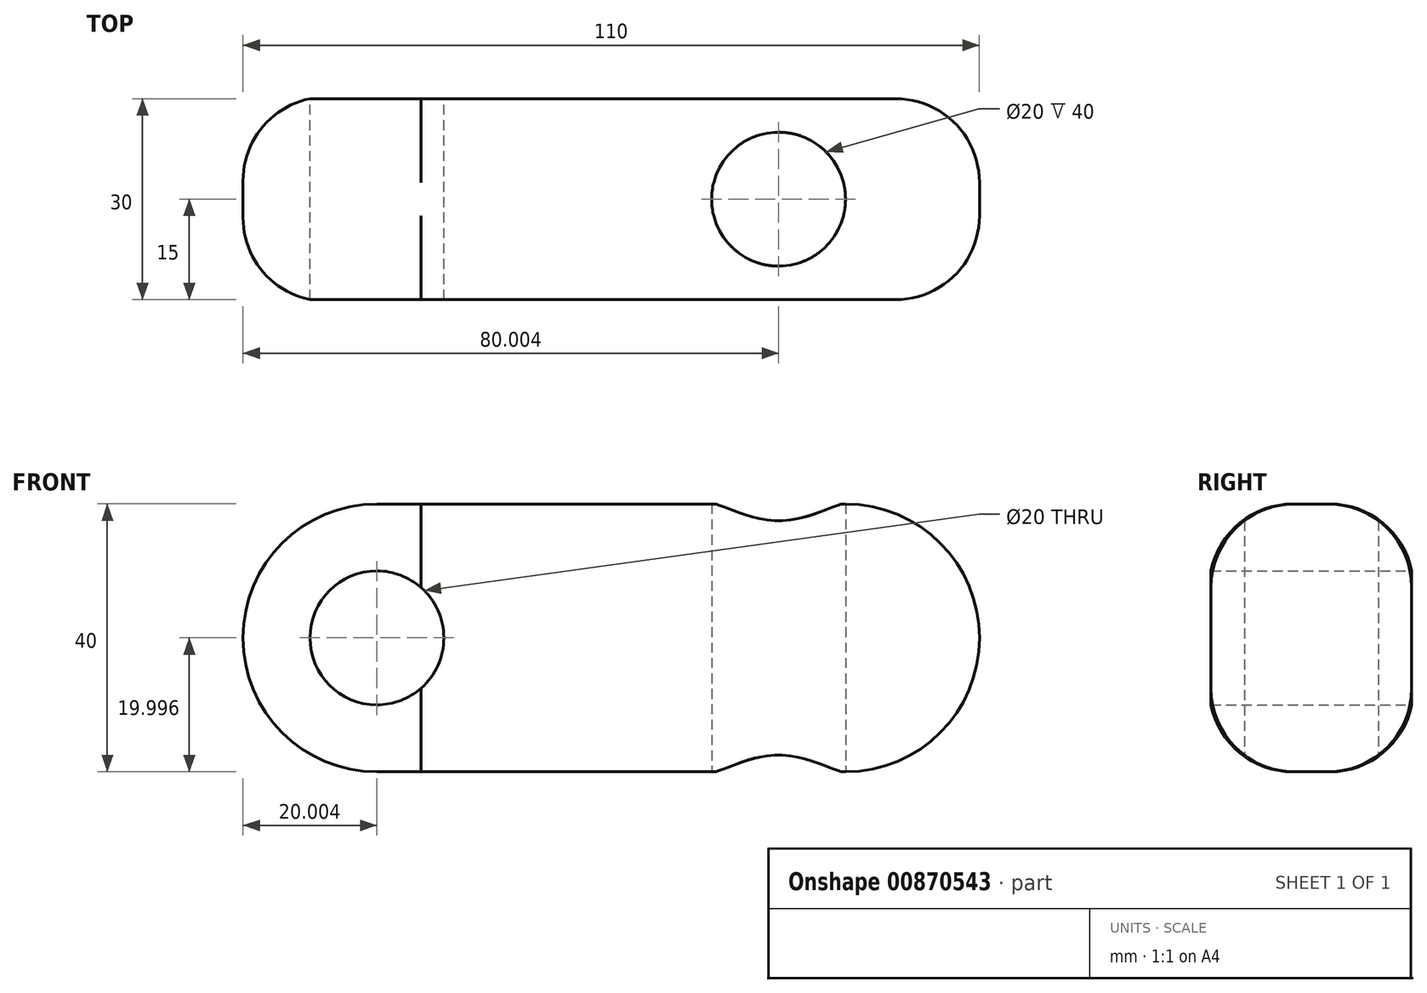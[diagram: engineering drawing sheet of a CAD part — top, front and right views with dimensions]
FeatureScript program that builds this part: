
annotation { "Feature Type Name" : "Feature", "Feature Type Description" : "" }
export const myFeature = defineFeature(function(context is Context, id is Id, definition is map)
    precondition{}
    {
        {
            var Q0;
            Q0=qCreatedBy(makeId("Front.planeOp"),FACE);
            var sketch = newSketch(context, id + "F0", { "sketchPlane" : qUnion([Q0])});
            skLineSegment(sketch, "E0.bottom", {"start": v(-58.02, 21.1) * mm, "end": v(11.98, 21.1) * mm});
            skLineSegment(sketch, "E0.top", {"start": v(-58.02, -18.9) * mm, "end": v(11.98, -18.9) * mm});
            skLineSegment(sketch, "E0.left", {"start": v(-78.02, 1.1) * mm, "end": v(-78.02, 1.1) * mm});
            skLineSegment(sketch, "E0.right", {"start": v(31.98, 1.1) * mm, "end": v(31.98, 1.1) * mm});
            skPoint(sketch, "E1", {"position": v(11.98, 0) * mm});
            skPoint(sketch, "E2.visualSharp", {"position": v(-78.02, 21.1) * mm});
            skArc(sketch, "E2.filletArc", {"start": v(-58.02, 21.1) * mm, "mid": v(-72.16, 15.25) * mm, "end": v(-78.02, 1.1) * mm});
            skPoint(sketch, "E3.visualSharp", {"position": v(-78.02, -18.9) * mm});
            skArc(sketch, "E3.filletArc", {"start": v(-78.02, 1.1) * mm, "mid": v(-72.16, -13.04) * mm, "end": v(-58.02, -18.9) * mm});
            skPoint(sketch, "E4.visualSharp", {"position": v(31.98, -18.9) * mm});
            skArc(sketch, "E4.filletArc", {"start": v(11.98, -18.9) * mm, "mid": v(26.13, -13.04) * mm, "end": v(31.98, 1.1) * mm});
            skPoint(sketch, "E5.visualSharp", {"position": v(31.98, 21.1) * mm});
            skArc(sketch, "E5.filletArc", {"start": v(31.98, 1.1) * mm, "mid": v(26.13, 15.25) * mm, "end": v(11.98, 21.1) * mm});
            skCircle(sketch, "E6", {"center": v(-58.02, 1.1) * mm, "radius": 10 * mm});
            skSolve(sketch);
        }
        {
            var Q0;
            Q0=makeQuery(id+"F0.imprint","IMPRINT",FACE,{"disambiguationData":[TD([[makeQuery(id+"F0.imprint","IMPRINT",EDGE,{"derivedFrom":sQuery(id+"F0.wireOp",EDGE,"E0.bottom")}),-1.0]])]});
            extrude(context, id + "F1", {"entities" : qUnion([Q0]), "depth" : 30 * mm, "offsetDistance" : 25 * mm});
        }
        {
            var Q0;
            Q0=makeQuery(id+"F1.opExtrude","SWEPT_FACE",FACE,{"disambiguationData":[OSD([sQuery(id+"F0.wireOp",EDGE,"E0.top")])]});
            var sketch = newSketch(context, id + "F2", { "sketchPlane" : qUnion([Q0])});
            skCircle(sketch, "E7", {"center": v(1.98, 15) * mm, "radius": 10 * mm});
            skPoint(sketch, "E7.centerSnap0", {"position": v(11.98, 15) * mm});
            skSolve(sketch);
        }
        {
            var Q0;
            Q0=makeQuery(id+"F1.opExtrude","CAP_EDGE",EDGE,{"disambiguationData":[OSD([sQuery(id+"F0.wireOp",EDGE,"E0.bottom")])],"isStart":true});
            var Q1;
            Q1=makeQuery(id+"F1.opExtrude","CAP_EDGE",EDGE,{"disambiguationData":[OSD([sQuery(id+"F0.wireOp",EDGE,"E0.bottom")])],"isStart":false});
            fillet(context, id + "F3", {"entities" : qUnion([Q0, Q1]), "radius" : 12.5 * mm, "tangentPropagation" : true, "allowEdgeOverflow" : false});
        }
        {
            var Q0;
            Q0=sQuery(id+"F2.wireOp",VERTEX,"E7.center");
            var Q1;
            Q1=makeQuery(id+"F1.opExtrude","SWEPT_BODY",BODY,{"disambiguationData":[OSD([sQuery(id+"F0.wireOp",EDGE,"E0.bottom"),sQuery(id+"F0.wireOp",EDGE,"E0.top"),sQuery(id+"F0.wireOp",EDGE,"E2.filletArc"),sQuery(id+"F0.wireOp",EDGE,"E3.filletArc"),sQuery(id+"F0.wireOp",EDGE,"E4.filletArc"),sQuery(id+"F0.wireOp",EDGE,"E5.filletArc"),sQuery(id+"F0.wireOp",EDGE,"E6")])]});
            hole(context, id + "F4", {"style" : HoleStyle.SIMPLE, "endStyle" : HoleEndStyle.THROUGH, "holeDiameter" : 20 * mm, "majorDiameter" : 5 * mm, "isTappedThrough" : true, "tappedDepth" : 12 * mm, "tapClearance" : 3, "locations" : qUnion([Q0]), "scope" : qUnion([Q1])});
        }
    });
